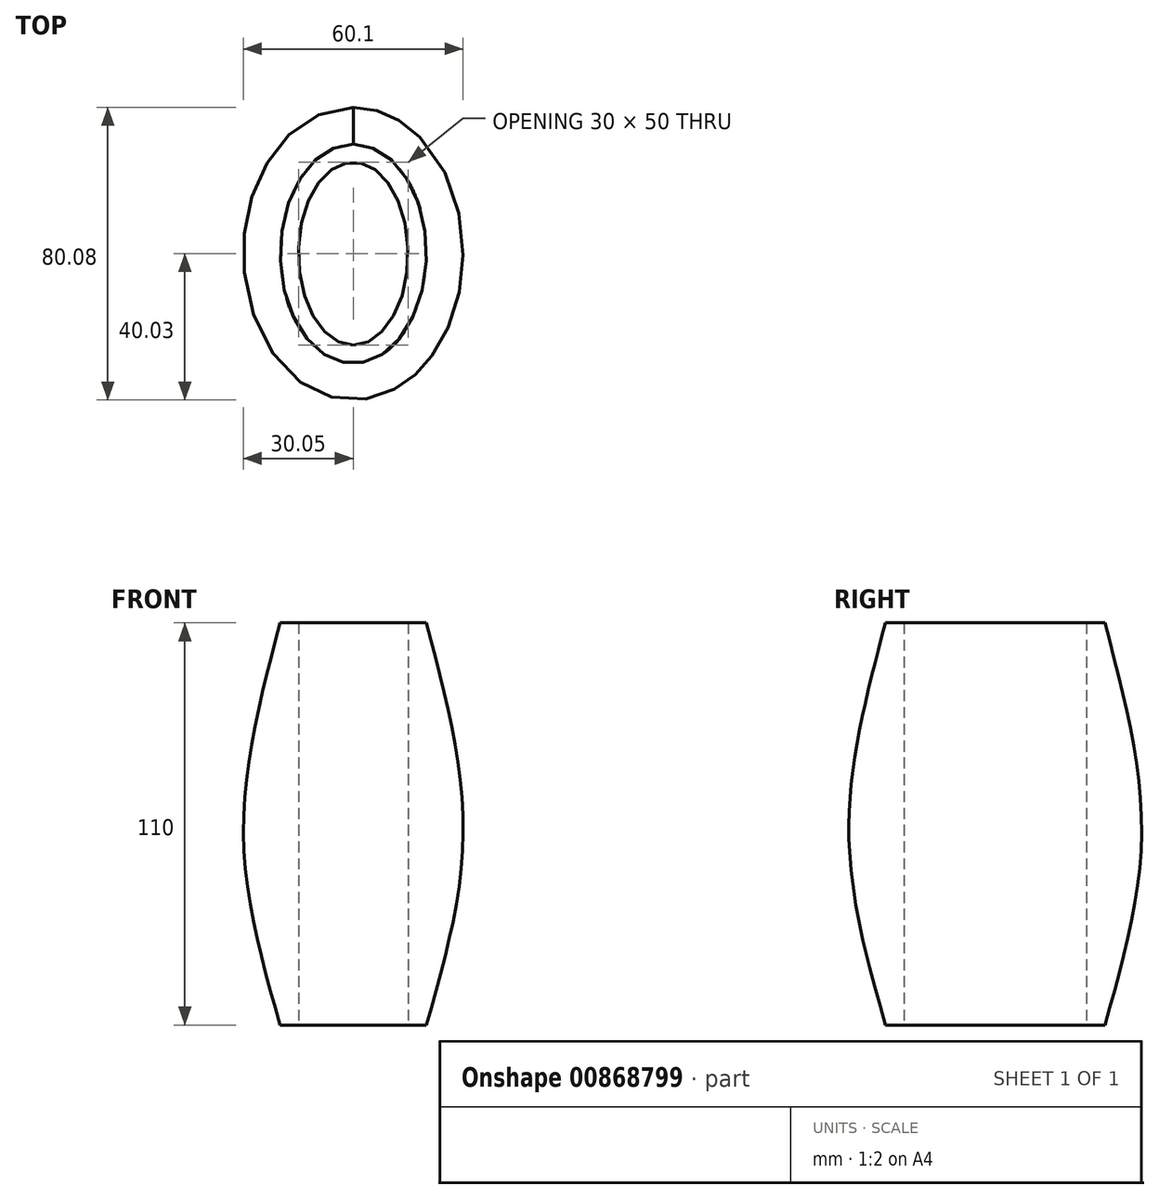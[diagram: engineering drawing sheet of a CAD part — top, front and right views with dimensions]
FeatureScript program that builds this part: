
annotation { "Feature Type Name" : "Feature", "Feature Type Description" : "" }
export const myFeature = defineFeature(function(context is Context, id is Id, definition is map)
    precondition{}
    {
        {
            var Q0;
            Q0=qCreatedBy(makeId("Top.planeOp"),FACE);
            var sketch = newSketch(context, id + "F0", { "sketchPlane" : qUnion([Q0])});
            skEllipse(sketch, "E0", {"center": v(0, 0) * mm, "majorRadius": 30 * mm, "minorRadius": 20 * mm, "majorAxis": v(0, 1)});
            skSolve(sketch);
        }
        {
            var Q0;
            Q0=makeQuery(id+"F0.imprint","IMPRINT",FACE,{"disambiguationData":[TD([[makeQuery(id+"F0.imprint","IMPRINT",EDGE,{"derivedFrom":sQuery(id+"F0.wireOp",EDGE,"E0")}),1.0]])]});
            extrude(context, id + "F1", {"entities" : qUnion([Q0]), "depth" : 110 * mm, "offsetDistance" : 25 * mm});
        }
        {
            var Q0;
            Q0=qCreatedBy(makeId("Top.planeOp"),FACE);
            cPlane(context, id + "F2", {"entities" : qUnion([Q0]), "cplaneType" : CPlaneType.OFFSET, "offset" : 50 * mm, "width" : 150 * mm, "height" : 150 * mm});
        }
        {
            var Q0;
            Q0=qCreatedBy(id+"F2.planeOp",FACE);
            var sketch = newSketch(context, id + "F3", { "sketchPlane" : qUnion([Q0])});
            skEllipse(sketch, "E1", {"center": v(0, 0) * mm, "majorRadius": 40 * mm, "minorRadius": 30 * mm, "majorAxis": v(0, 1)});
            skSolve(sketch);
        }
        {
            var Q1;
            Q1=makeQuery(id+"F1.opExtrude","CAP_FACE",FACE,{"disambiguationData":[OSD([sQuery(id+"F0.wireOp",EDGE,"E0")])],"isStart":true});
            var Q2;
            Q2=makeQuery(id+"F3.imprint","IMPRINT",FACE,{"disambiguationData":[TD([[makeQuery(id+"F3.imprint","IMPRINT",EDGE,{"derivedFrom":sQuery(id+"F3.wireOp",EDGE,"E1")}),1.0]])]});
            var Q3;
            Q3=makeQuery(id+"F1.opExtrude","CAP_FACE",FACE,{"disambiguationData":[OSD([sQuery(id+"F0.wireOp",EDGE,"E0")])],"isStart":false});
            loft(context, id + "F4", {"operationType" : NewBodyOperationType.ADD, "sheetProfilesArray" : [{ "sheetProfileEntities" : qUnion([Q1]) }, { "sheetProfileEntities" : qUnion([Q2]) }, { "sheetProfileEntities" : qUnion([Q3]) }]});
        }
        {
            var Q0;
            Q0=qCreatedBy(makeId("Top.planeOp"),FACE);
            var sketch = newSketch(context, id + "F5", { "sketchPlane" : qUnion([Q0])});
            skEllipse(sketch, "E2", {"center": v(0, 0) * mm, "majorRadius": 25 * mm, "minorRadius": 15 * mm, "majorAxis": v(0, -1)});
            skSolve(sketch);
        }
        {
            var Q0;
            Q0=makeQuery(id+"F5.imprint","IMPRINT",FACE,{"disambiguationData":[TD([[makeQuery(id+"F5.imprint","IMPRINT",EDGE,{"derivedFrom":sQuery(id+"F5.wireOp",EDGE,"E2")}),1.0]])]});
            extrude(context, id + "F6", {"entities" : qUnion([Q0]), "operationType" : NewBodyOperationType.REMOVE, "depth" : 110 * mm, "offsetDistance" : 25 * mm});
        }
    });
